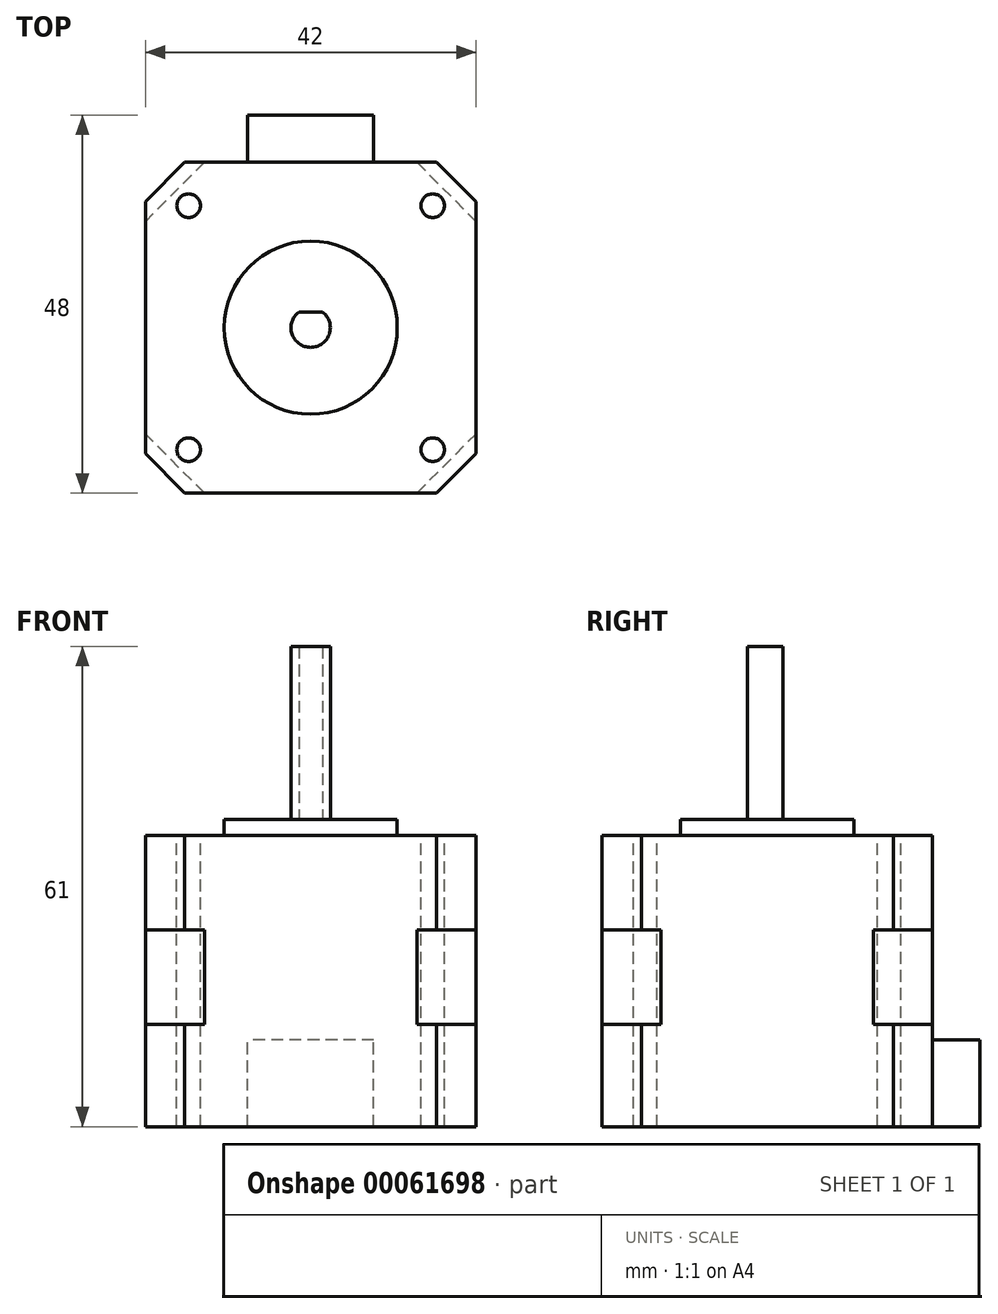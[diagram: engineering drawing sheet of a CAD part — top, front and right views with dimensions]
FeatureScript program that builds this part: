
annotation { "Feature Type Name" : "Feature", "Feature Type Description" : "" }
export const myFeature = defineFeature(function(context is Context, id is Id, definition is map)
    precondition{}
    {
        {
            var Q0;
            Q0=qCreatedBy(makeId("Top.planeOp"),FACE);
            var sketch = newSketch(context, id + "F0", { "sketchPlane" : qUnion([Q0])});
            skLineSegment(sketch, "E0.bottom", {"start": v(-21, 21) * mm, "end": v(21, 21) * mm});
            skLineSegment(sketch, "E0.top", {"start": v(-21, -21) * mm, "end": v(21, -21) * mm});
            skLineSegment(sketch, "E0.left", {"start": v(-21, 21) * mm, "end": v(-21, -21) * mm});
            skLineSegment(sketch, "E0.right", {"start": v(21, 21) * mm, "end": v(21, -21) * mm});
            skSolve(sketch);
        }
        {
            var Q0;
            Q0=makeQuery(id+"F0.imprint","IMPRINT",FACE,{"disambiguationData":[TD([[makeQuery(id+"F0.imprint","IMPRINT",EDGE,{"derivedFrom":sQuery(id+"F0.wireOp",EDGE,"E0.bottom")}),-1.0]])]});
            extrude(context, id + "F1", {"entities" : qUnion([Q0]), "endBound" : BoundingType.SYMMETRIC, "depth" : 12 * mm});
        }
        {
            var Q0;
            Q0=makeQuery(id+"F1.opExtrude","SWEPT_EDGE",EDGE,{"disambiguationData":[OSD([sQuery(id+"F0.wireOp",EDGE,"E0.bottom"),sQuery(id+"F0.wireOp",EDGE,"E0.right")])]});
            var Q1;
            Q1=makeQuery(id+"F1.opExtrude","SWEPT_EDGE",EDGE,{"disambiguationData":[OSD([sQuery(id+"F0.wireOp",EDGE,"E0.bottom"),sQuery(id+"F0.wireOp",EDGE,"E0.left")])]});
            var Q2;
            Q2=makeQuery(id+"F1.opExtrude","SWEPT_EDGE",EDGE,{"disambiguationData":[OSD([sQuery(id+"F0.wireOp",EDGE,"E0.top"),sQuery(id+"F0.wireOp",EDGE,"E0.left")])]});
            var Q3;
            Q3=makeQuery(id+"F1.opExtrude","SWEPT_EDGE",EDGE,{"disambiguationData":[OSD([sQuery(id+"F0.wireOp",EDGE,"E0.top"),sQuery(id+"F0.wireOp",EDGE,"E0.right")])]});
            chamfer(context, id + "F2", {"entities" : qUnion([Q0, Q1, Q2, Q3]), "width" : 7.5 * mm, "tangentPropagation" : true});
        }
        {
            var Q0;
            Q0=makeQuery(id+"F1.opExtrude","CAP_FACE",FACE,{"disambiguationData":[OSD([sQuery(id+"F0.wireOp",EDGE,"E0.bottom"),sQuery(id+"F0.wireOp",EDGE,"E0.top"),sQuery(id+"F0.wireOp",EDGE,"E0.left"),sQuery(id+"F0.wireOp",EDGE,"E0.right")])],"isStart":false});
            var sketch = newSketch(context, id + "F3", { "sketchPlane" : qUnion([Q0])});
            skLineSegment(sketch, "E1.0", {"start": v(-21, 21) * mm, "end": v(21, 21) * mm});
            skLineSegment(sketch, "E1.1", {"start": v(-21, 21) * mm, "end": v(-21, -21) * mm});
            skLineSegment(sketch, "E1.2", {"start": v(-21, -21) * mm, "end": v(21, -21) * mm});
            skLineSegment(sketch, "E1.3", {"start": v(21, 21) * mm, "end": v(21, -21) * mm});
            skSolve(sketch);
        }
        {
            var Q0;
            {var subQ0=sQuery(id+"F0.wireOp",EDGE,"E0.top");var subQ1=sQuery(id+"F0.wireOp",EDGE,"E0.right");var subQ2=sQuery(id+"F0.wireOp",EDGE,"E0.bottom");var subQ3=sQuery(id+"F0.wireOp",EDGE,"E0.left");var subQ4=makeQuery(id+"F1.opExtrude","CAP_FACE",FACE,{"disambiguationData":[OSD([subQ2,subQ0,subQ3,subQ1])],"isStart":false});var subQ8=makeQuery(id+"F2.opChamfer","BLEND_EDGE",EDGE,{"blendedFrom":[makeQuery(id+"F1.opExtrude","SWEPT_EDGE",EDGE,{"disambiguationData":[OSD([subQ2,subQ3])]}),subQ4],"blendedInto":[subQ4]});Q0=makeQuery(id+"F3.imprint","IMPRINT",FACE,{"disambiguationData":[TD([[makeQuery(id+"F3.imprint","IMPRINT",EDGE,{"derivedFrom":subQ8}),1.0]])]});}
            var Q1;
            {var subQ0=sQuery(id+"F0.wireOp",EDGE,"E0.bottom");var subQ1=sQuery(id+"F0.wireOp",EDGE,"E0.right");var subQ2=makeQuery(id+"F2.opChamfer","BLEND_EDGE",EDGE,{"blendedFrom":[makeQuery(id+"F1.opExtrude","SWEPT_EDGE",EDGE,{"disambiguationData":[OSD([subQ0,subQ1])]}),makeQuery(id+"F1.opExtrude","CAP_FACE",FACE,{"disambiguationData":[OSD([subQ0,sQuery(id+"F0.wireOp",EDGE,"E0.top"),sQuery(id+"F0.wireOp",EDGE,"E0.left"),subQ1])],"isStart":false})],"blendedInto":[makeQuery(id+"F1.opExtrude","CAP_FACE",FACE,{"disambiguationData":[OSD([subQ0,sQuery(id+"F0.wireOp",EDGE,"E0.top"),sQuery(id+"F0.wireOp",EDGE,"E0.left"),subQ1])],"isStart":false})]});Q1=makeQuery(id+"F3.imprint","IMPRINT",FACE,{"disambiguationData":[TD([[makeQuery(id+"F3.imprint","IMPRINT",EDGE,{"derivedFrom":subQ2}),-1.0]])]});}
            var Q2;
            {var subQ0=sQuery(id+"F0.wireOp",EDGE,"E0.bottom");var subQ1=sQuery(id+"F0.wireOp",EDGE,"E0.left");var subQ2=makeQuery(id+"F2.opChamfer","BLEND_EDGE",EDGE,{"blendedFrom":[makeQuery(id+"F1.opExtrude","SWEPT_EDGE",EDGE,{"disambiguationData":[OSD([subQ0,subQ1])]}),makeQuery(id+"F1.opExtrude","CAP_FACE",FACE,{"disambiguationData":[OSD([subQ0,sQuery(id+"F0.wireOp",EDGE,"E0.top"),subQ1,sQuery(id+"F0.wireOp",EDGE,"E0.right")])],"isStart":false})],"blendedInto":[makeQuery(id+"F1.opExtrude","CAP_FACE",FACE,{"disambiguationData":[OSD([subQ0,sQuery(id+"F0.wireOp",EDGE,"E0.top"),subQ1,sQuery(id+"F0.wireOp",EDGE,"E0.right")])],"isStart":false})]});Q2=makeQuery(id+"F3.imprint","IMPRINT",FACE,{"disambiguationData":[TD([[makeQuery(id+"F3.imprint","IMPRINT",EDGE,{"derivedFrom":subQ2}),-1.0]])]});}
            var Q3;
            {var subQ0=sQuery(id+"F0.wireOp",EDGE,"E0.top");var subQ1=sQuery(id+"F0.wireOp",EDGE,"E0.left");var subQ2=makeQuery(id+"F2.opChamfer","BLEND_EDGE",EDGE,{"blendedFrom":[makeQuery(id+"F1.opExtrude","SWEPT_EDGE",EDGE,{"disambiguationData":[OSD([subQ0,subQ1])]}),makeQuery(id+"F1.opExtrude","CAP_FACE",FACE,{"disambiguationData":[OSD([sQuery(id+"F0.wireOp",EDGE,"E0.bottom"),subQ0,subQ1,sQuery(id+"F0.wireOp",EDGE,"E0.right")])],"isStart":false})],"blendedInto":[makeQuery(id+"F1.opExtrude","CAP_FACE",FACE,{"disambiguationData":[OSD([sQuery(id+"F0.wireOp",EDGE,"E0.bottom"),subQ0,subQ1,sQuery(id+"F0.wireOp",EDGE,"E0.right")])],"isStart":false})]});Q3=makeQuery(id+"F3.imprint","IMPRINT",FACE,{"disambiguationData":[TD([[makeQuery(id+"F3.imprint","IMPRINT",EDGE,{"derivedFrom":subQ2}),-1.0]])]});}
            var Q4;
            {var subQ0=sQuery(id+"F0.wireOp",EDGE,"E0.top");var subQ1=sQuery(id+"F0.wireOp",EDGE,"E0.right");var subQ2=makeQuery(id+"F2.opChamfer","BLEND_EDGE",EDGE,{"blendedFrom":[makeQuery(id+"F1.opExtrude","SWEPT_EDGE",EDGE,{"disambiguationData":[OSD([subQ0,subQ1])]}),makeQuery(id+"F1.opExtrude","CAP_FACE",FACE,{"disambiguationData":[OSD([sQuery(id+"F0.wireOp",EDGE,"E0.bottom"),subQ0,sQuery(id+"F0.wireOp",EDGE,"E0.left"),subQ1])],"isStart":false})],"blendedInto":[makeQuery(id+"F1.opExtrude","CAP_FACE",FACE,{"disambiguationData":[OSD([sQuery(id+"F0.wireOp",EDGE,"E0.bottom"),subQ0,sQuery(id+"F0.wireOp",EDGE,"E0.left"),subQ1])],"isStart":false})]});Q4=makeQuery(id+"F3.imprint","IMPRINT",FACE,{"disambiguationData":[TD([[makeQuery(id+"F3.imprint","IMPRINT",EDGE,{"derivedFrom":subQ2}),-1.0]])]});}
            extrude(context, id + "F4", {"entities" : qUnion([Q0, Q1, Q2, Q3, Q4]), "operationType" : NewBodyOperationType.ADD, "depth" : 12 * mm});
        }
        {
            var Q0;
            Q0=makeQuery(id+"F4.opExtrude","SWEPT_EDGE",EDGE,{"disambiguationData":[OSD([sQuery(id+"F3.wireOp",EDGE,"E1.2"),sQuery(id+"F3.wireOp",EDGE,"E1.3")])]});
            var Q1;
            Q1=makeQuery(id+"F4.opExtrude","SWEPT_EDGE",EDGE,{"disambiguationData":[OSD([sQuery(id+"F3.wireOp",EDGE,"E1.1"),sQuery(id+"F3.wireOp",EDGE,"E1.2")])]});
            var Q2;
            Q2=makeQuery(id+"F4.opExtrude","SWEPT_EDGE",EDGE,{"disambiguationData":[OSD([sQuery(id+"F3.wireOp",EDGE,"E1.0"),sQuery(id+"F3.wireOp",EDGE,"E1.1")])]});
            var Q3;
            Q3=makeQuery(id+"F4.opExtrude","SWEPT_EDGE",EDGE,{"disambiguationData":[OSD([sQuery(id+"F3.wireOp",EDGE,"E1.0"),sQuery(id+"F3.wireOp",EDGE,"E1.3")])]});
            chamfer(context, id + "F5", {"entities" : qUnion([Q0, Q1, Q2, Q3]), "width" : 5 * mm, "tangentPropagation" : true});
        }
        {
            var Q0;
            Q0=makeQuery(id+"F1.opExtrude","CAP_FACE",FACE,{"disambiguationData":[OSD([sQuery(id+"F0.wireOp",EDGE,"E0.bottom"),sQuery(id+"F0.wireOp",EDGE,"E0.top"),sQuery(id+"F0.wireOp",EDGE,"E0.left"),sQuery(id+"F0.wireOp",EDGE,"E0.right")])],"isStart":true});
            var sketch = newSketch(context, id + "F6", { "sketchPlane" : qUnion([Q0])});
            skLineSegment(sketch, "E2.0.0", {"start": v(21, 16) * mm, "end": v(21, -16) * mm});
            skLineSegment(sketch, "E2.0.1", {"start": v(21, -16) * mm, "end": v(16, -21) * mm});
            skLineSegment(sketch, "E2.0.2", {"start": v(16, -21) * mm, "end": v(-16, -21) * mm});
            skLineSegment(sketch, "E2.0.3", {"start": v(-16, -21) * mm, "end": v(-21, -16) * mm});
            skLineSegment(sketch, "E2.0.4", {"start": v(-21, -16) * mm, "end": v(-21, 16) * mm});
            skLineSegment(sketch, "E2.0.5", {"start": v(-21, 16) * mm, "end": v(-16, 21) * mm});
            skLineSegment(sketch, "E2.0.6", {"start": v(-16, 21) * mm, "end": v(16, 21) * mm});
            skLineSegment(sketch, "E2.0.7", {"start": v(16, 21) * mm, "end": v(21, 16) * mm});
            skSolve(sketch);
        }
        {
            var Q0;
            Q0=qSketchRegion(id+"F6",true);
            extrude(context, id + "F7", {"entities" : qUnion([Q0]), "operationType" : NewBodyOperationType.ADD, "depth" : 13 * mm});
        }
        {
            var Q0;
            Q0=makeQuery(id+"F4.opExtrude","CAP_FACE",FACE,{"disambiguationData":[OSD([sQuery(id+"F3.wireOp",EDGE,"E1.0"),sQuery(id+"F3.wireOp",EDGE,"E1.1"),sQuery(id+"F3.wireOp",EDGE,"E1.2"),sQuery(id+"F3.wireOp",EDGE,"E1.3")])],"isStart":false});
            var sketch = newSketch(context, id + "F8", { "sketchPlane" : qUnion([Q0])});
            skCircle(sketch, "E3", {"center": v(0, 0) * mm, "radius": 11 * mm});
            skSolve(sketch);
        }
        {
            var Q0;
            Q0=qSketchRegion(id+"F8",true);
            extrude(context, id + "F9", {"entities" : qUnion([Q0]), "operationType" : NewBodyOperationType.ADD, "depth" : 2 * mm});
        }
        {
            var Q0;
            Q0=makeQuery(id+"F9.opExtrude","CAP_FACE",FACE,{"disambiguationData":[OSD([sQuery(id+"F8.wireOp",EDGE,"E3")])],"isStart":false});
            var sketch = newSketch(context, id + "F10", { "sketchPlane" : qUnion([Q0])});
            skCircle(sketch, "E4", {"center": v(0, 0) * mm, "radius": 2.5 * mm});
            skSolve(sketch);
        }
        {
            var Q0;
            Q0=makeQuery(id+"F10.imprint","IMPRINT",FACE,{"disambiguationData":[TD([[makeQuery(id+"F10.imprint","IMPRINT",EDGE,{"derivedFrom":sQuery(id+"F10.wireOp",EDGE,"E4")}),1.0]])]});
            extrude(context, id + "F11", {"entities" : qUnion([Q0]), "operationType" : NewBodyOperationType.ADD, "depth" : 22 * mm});
        }
        {
            var Q0;
            Q0=makeQuery(id+"F11.opExtrude","CAP_FACE",FACE,{"disambiguationData":[OSD([sQuery(id+"F10.wireOp",EDGE,"E4")])],"isStart":false});
            var sketch = newSketch(context, id + "F12", { "sketchPlane" : qUnion([Q0])});
            skLineSegment(sketch, "E5.bottom", {"start": v(-2.63, 2.93) * mm, "end": v(2.62, 2.93) * mm});
            skLineSegment(sketch, "E5.top", {"start": v(-2.63, 2) * mm, "end": v(2.62, 2) * mm});
            skLineSegment(sketch, "E5.left", {"start": v(-2.63, 2.93) * mm, "end": v(-2.63, 2) * mm});
            skLineSegment(sketch, "E5.right", {"start": v(2.62, 2.93) * mm, "end": v(2.62, 2) * mm});
            skSolve(sketch);
        }
        {
            var Q0;
            Q0=qSketchRegion(id+"F12",true);
            extrude(context, id + "F13", {"entities" : qUnion([Q0]), "operationType" : NewBodyOperationType.REMOVE, "oppositeDirection" : true, "depth" : 22 * mm});
        }
        {
            var Q0;
            Q0=makeQuery(id+"F4.opExtrude","CAP_FACE",FACE,{"disambiguationData":[OSD([sQuery(id+"F3.wireOp",EDGE,"E1.0"),sQuery(id+"F3.wireOp",EDGE,"E1.1"),sQuery(id+"F3.wireOp",EDGE,"E1.2"),sQuery(id+"F3.wireOp",EDGE,"E1.3")])],"isStart":false});
            var sketch = newSketch(context, id + "F14", { "sketchPlane" : qUnion([Q0])});
            skCircle(sketch, "E6", {"center": v(-15.5, 15.5) * mm, "radius": 1.5 * mm});
            skCircle(sketch, "E7.MirrorC", {"center": v(15.5, 15.5) * mm, "radius": 1.5 * mm});
            skCircle(sketch, "E8.MirrorC", {"center": v(-15.5, -15.5) * mm, "radius": 1.5 * mm});
            skCircle(sketch, "E9.MirrorC", {"center": v(15.5, -15.5) * mm, "radius": 1.5 * mm});
            skSolve(sketch);
        }
        {
            var Q0;
            Q0=qSketchRegion(id+"F14",true);
            extrude(context, id + "F15", {"entities" : qUnion([Q0]), "operationType" : NewBodyOperationType.REMOVE, "endBound" : BoundingType.THROUGH_ALL, "oppositeDirection" : true, "depth" : 6 * mm});
        }
        {
            var Q0;
            Q0=makeQuery(id+"F7.boolean.opBoolean","MERGE",FACE,{"derivedFrom":[makeQuery(id+"F4.boolean.opBoolean","MERGE",FACE,{"derivedFrom":[makeQuery(id+"F1.opExtrude","SWEPT_FACE",FACE,{"disambiguationData":[OSD([sQuery(id+"F0.wireOp",EDGE,"E0.bottom")])]}),makeQuery(id+"F4.opExtrude","SWEPT_FACE",FACE,{"disambiguationData":[OSD([sQuery(id+"F3.wireOp",EDGE,"E1.0")])]})]}),makeQuery(id+"F7.opExtrude","SWEPT_FACE",FACE,{"disambiguationData":[OSD([sQuery(id+"F6.wireOp",EDGE,"E2.0.2")])]})]});
            var sketch = newSketch(context, id + "F16", { "sketchPlane" : qUnion([Q0])});
            skLineSegment(sketch, "E10.bottom", {"start": v(-8, -19) * mm, "end": v(8, -19) * mm});
            skLineSegment(sketch, "E10.top", {"start": v(-8, -8) * mm, "end": v(8, -8) * mm});
            skLineSegment(sketch, "E10.left", {"start": v(-8, -19) * mm, "end": v(-8, -8) * mm});
            skLineSegment(sketch, "E10.right", {"start": v(8, -19) * mm, "end": v(8, -8) * mm});
            skLineSegment(sketch, "E11", {"start": v(0, -8) * mm, "end": v(0, 0) * mm, "construction": true});
            skSolve(sketch);
        }
        {
            var Q0;
            Q0 = qSketchRegion(id + "F16", true);
            extrude(context, id + "F17", {"entities" : qUnion([Q0]), "operationType" : NewBodyOperationType.ADD, "depth" : 6 * mm});
        }
    });
